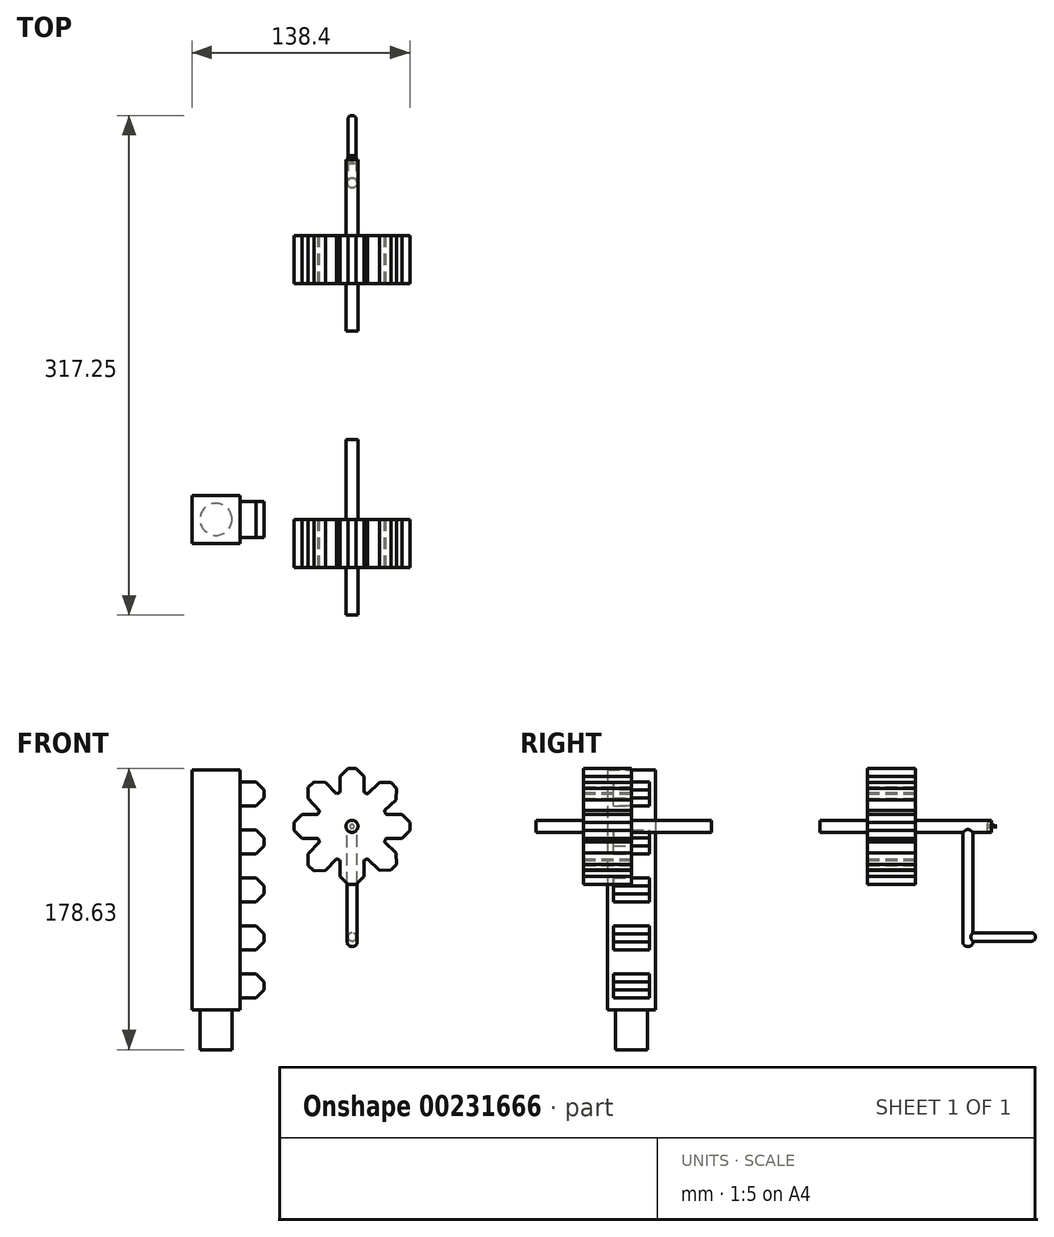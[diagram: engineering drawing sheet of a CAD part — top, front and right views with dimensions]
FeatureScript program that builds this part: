
annotation { "Feature Type Name" : "Feature", "Feature Type Description" : "" }
export const myFeature = defineFeature(function(context is Context, id is Id, definition is map)
    precondition{}
    {
        {
            var Q0;
            Q0=qCreatedBy(makeId("Top.planeOp"),FACE);
            var sketch = newSketch(context, id + "F0", { "sketchPlane" : qUnion([Q0])});
            skLineSegment(sketch, "E0.bottom", {"start": v(-15.24, -15.24) * mm, "end": v(15.24, -15.24) * mm});
            skLineSegment(sketch, "E0.top", {"start": v(-15.24, 15.24) * mm, "end": v(15.24, 15.24) * mm});
            skLineSegment(sketch, "E0.left", {"start": v(-15.24, -15.24) * mm, "end": v(-15.24, 15.24) * mm});
            skLineSegment(sketch, "E0.right", {"start": v(15.24, -15.24) * mm, "end": v(15.24, 15.24) * mm});
            skPoint(sketch, "E0.middle", {"position": v(0, 0) * mm});
            skCircle(sketch, "E1", {"center": v(0, 0) * mm, "radius": 10.16 * mm});
            skSolve(sketch);
        }
        {
            var Q0;
            Q0=makeQuery(id+"F0.imprint","IMPRINT",FACE,{"disambiguationData":[TD([[makeQuery(id+"F0.imprint","IMPRINT",EDGE,{"derivedFrom":sQuery(id+"F0.wireOp",EDGE,"E0.bottom")}),1.0]])]});
            var Q1;
            Q1=makeQuery(id+"F0.imprint","IMPRINT",FACE,{"disambiguationData":[TD([[makeQuery(id+"F0.imprint","IMPRINT",EDGE,{"derivedFrom":sQuery(id+"F0.wireOp",EDGE,"E1")}),1.0]])]});
            extrude(context, id + "F1", {"entities" : qUnion([Q0, Q1]), "depth" : 152.4 * mm});
        }
        {
            var Q0;
            Q0=makeQuery(id+"F0.imprint","IMPRINT",FACE,{"disambiguationData":[TD([[makeQuery(id+"F0.imprint","IMPRINT",EDGE,{"derivedFrom":sQuery(id+"F0.wireOp",EDGE,"E1")}),1.0]])]});
            extrude(context, id + "F2", {"entities" : qUnion([Q0]), "operationType" : NewBodyOperationType.ADD, "oppositeDirection" : true, "depth" : 25.4 * mm});
        }
        {
            var Q0;
            Q0=qCreatedBy(makeId("Right.planeOp"),FACE);
            var sketch = newSketch(context, id + "F3", { "sketchPlane" : qUnion([Q0])});
            skLineSegment(sketch, "E2.bottom", {"start": v(-11.43, 7.62) * mm, "end": v(11.43, 7.62) * mm});
            skLineSegment(sketch, "E2.top", {"start": v(-11.43, 22.86) * mm, "end": v(11.43, 22.86) * mm});
            skLineSegment(sketch, "E2.left", {"start": v(-11.43, 7.62) * mm, "end": v(-11.43, 22.86) * mm});
            skLineSegment(sketch, "E2.right", {"start": v(11.43, 7.62) * mm, "end": v(11.43, 22.86) * mm});
            skPoint(sketch, "E2.middle", {"position": v(0, 15.24) * mm});
            skLineSegment(sketch, "E3.0.1.0", {"start": v(-11.43, 53.34) * mm, "end": v(11.43, 53.34) * mm});
            skLineSegment(sketch, "E3.0.1.1", {"start": v(-11.43, 38.1) * mm, "end": v(-11.43, 53.34) * mm});
            skLineSegment(sketch, "E3.0.1.2", {"start": v(11.43, 38.1) * mm, "end": v(11.43, 53.34) * mm});
            skLineSegment(sketch, "E3.0.1.3", {"start": v(-11.43, 38.1) * mm, "end": v(11.43, 38.1) * mm});
            skLineSegment(sketch, "E3.0.2.0", {"start": v(-11.43, 83.82) * mm, "end": v(11.43, 83.82) * mm});
            skLineSegment(sketch, "E3.0.2.1", {"start": v(-11.43, 68.58) * mm, "end": v(-11.43, 83.82) * mm});
            skLineSegment(sketch, "E3.0.2.2", {"start": v(11.43, 68.58) * mm, "end": v(11.43, 83.82) * mm});
            skLineSegment(sketch, "E3.0.2.3", {"start": v(-11.43, 68.58) * mm, "end": v(11.43, 68.58) * mm});
            skLineSegment(sketch, "E3.0.3.0", {"start": v(-11.43, 114.3) * mm, "end": v(11.43, 114.3) * mm});
            skLineSegment(sketch, "E3.0.3.1", {"start": v(-11.43, 99.06) * mm, "end": v(-11.43, 114.3) * mm});
            skLineSegment(sketch, "E3.0.3.2", {"start": v(11.43, 99.06) * mm, "end": v(11.43, 114.3) * mm});
            skLineSegment(sketch, "E3.0.3.3", {"start": v(-11.43, 99.06) * mm, "end": v(11.43, 99.06) * mm});
            skLineSegment(sketch, "E3.0.4.0", {"start": v(-11.43, 144.78) * mm, "end": v(11.43, 144.78) * mm});
            skLineSegment(sketch, "E3.0.4.1", {"start": v(-11.43, 129.54) * mm, "end": v(-11.43, 144.78) * mm});
            skLineSegment(sketch, "E3.0.4.2", {"start": v(11.43, 129.54) * mm, "end": v(11.43, 144.78) * mm});
            skLineSegment(sketch, "E3.0.4.3", {"start": v(-11.43, 129.54) * mm, "end": v(11.43, 129.54) * mm});
            skLineSegment(sketch, "E3.direction1", {"start": v(-11.43, 22.86) * mm, "end": v(13.97, 22.86) * mm, "construction": true});
            skLineSegment(sketch, "E3.direction2", {"start": v(-11.43, 38.1) * mm, "end": v(-11.43, 53.34) * mm, "construction": true});
            skSolve(sketch);
        }
        {
            var Q0;
            Q0 = qSketchRegion(id + "F3", true);
            extrude(context, id + "F4", {"entities" : qUnion([Q0]), "operationType" : NewBodyOperationType.ADD, "depth" : 30.48 * mm});
        }
        {
            var Q0;
            Q0=makeQuery(id+"F4.opExtrude","CAP_EDGE",EDGE,{"disambiguationData":[OSD([sQuery(id+"F3.wireOp",EDGE,"E2.top")])],"isStart":false});
            var Q1;
            Q1=makeQuery(id+"F4.opExtrude","CAP_EDGE",EDGE,{"disambiguationData":[OSD([sQuery(id+"F3.wireOp",EDGE,"E2.bottom")])],"isStart":false});
            var Q2;
            Q2=makeQuery(id+"F4.opExtrude","CAP_EDGE",EDGE,{"disambiguationData":[OSD([sQuery(id+"F3.wireOp",EDGE,"E3.0.1.0")])],"isStart":false});
            var Q3;
            Q3=makeQuery(id+"F4.opExtrude","CAP_EDGE",EDGE,{"disambiguationData":[OSD([sQuery(id+"F3.wireOp",EDGE,"E3.0.1.3")])],"isStart":false});
            var Q4;
            Q4=makeQuery(id+"F4.opExtrude","CAP_EDGE",EDGE,{"disambiguationData":[OSD([sQuery(id+"F3.wireOp",EDGE,"E3.0.2.0")])],"isStart":false});
            var Q5;
            Q5=makeQuery(id+"F4.opExtrude","CAP_EDGE",EDGE,{"disambiguationData":[OSD([sQuery(id+"F3.wireOp",EDGE,"E3.0.2.3")])],"isStart":false});
            var Q6;
            Q6=makeQuery(id+"F4.opExtrude","CAP_EDGE",EDGE,{"disambiguationData":[OSD([sQuery(id+"F3.wireOp",EDGE,"E3.0.3.0")])],"isStart":false});
            var Q7;
            Q7=makeQuery(id+"F4.opExtrude","CAP_EDGE",EDGE,{"disambiguationData":[OSD([sQuery(id+"F3.wireOp",EDGE,"E3.0.3.3")])],"isStart":false});
            var Q8;
            Q8=makeQuery(id+"F4.opExtrude","CAP_EDGE",EDGE,{"disambiguationData":[OSD([sQuery(id+"F3.wireOp",EDGE,"E3.0.4.0")])],"isStart":false});
            var Q9;
            Q9=makeQuery(id+"F4.opExtrude","CAP_EDGE",EDGE,{"disambiguationData":[OSD([sQuery(id+"F3.wireOp",EDGE,"E3.0.4.3")])],"isStart":false});
            chamfer(context, id + "F5", {"entities" : qUnion([Q0, Q1, Q2, Q3, Q4, Q5, Q6, Q7, Q8, Q9]), "width" : 5.08 * mm, "tangentPropagation" : true});
        }
        {
            var Q0;
            Q0=qCreatedBy(makeId("Front.planeOp"),FACE);
            var sketch = newSketch(context, id + "F6", { "sketchPlane" : qUnion([Q0])});
            skCircle(sketch, "E4", {"center": v(86.36, 116.44) * mm, "radius": 22.86 * mm});
            skLineSegment(sketch, "E5", {"start": v(93.98, 138) * mm, "end": v(93.98, 153.23) * mm});
            skLineSegment(sketch, "E6", {"start": v(93.98, 153.23) * mm, "end": v(78.74, 153.23) * mm});
            skLineSegment(sketch, "E7", {"start": v(78.74, 153.23) * mm, "end": v(78.74, 138) * mm});
            skLineSegment(sketch, "E8", {"start": v(86.36, 116.44) * mm, "end": v(41.12, 116.44) * mm, "construction": true});
            skLineSegment(sketch, "E9", {"start": v(41.12, 116.44) * mm, "end": v(122.57, 116.44) * mm, "construction": true});
            skLineSegment(sketch, "E10.MirrorCS", {"start": v(93.98, 79.65) * mm, "end": v(78.74, 79.65) * mm});
            skLineSegment(sketch, "E11.MirrorCS", {"start": v(78.74, 79.65) * mm, "end": v(78.74, 94.89) * mm});
            skLineSegment(sketch, "E12.MirrorCS", {"start": v(93.98, 94.89) * mm, "end": v(93.98, 79.65) * mm});
            skLineSegment(sketch, "E13", {"start": v(64.8, 124) * mm, "end": v(49.55, 124) * mm});
            skLineSegment(sketch, "E14", {"start": v(49.55, 124) * mm, "end": v(49.55, 108.76) * mm});
            skLineSegment(sketch, "E15", {"start": v(49.55, 108.76) * mm, "end": v(64.83, 108.76) * mm});
            skLineSegment(sketch, "E16", {"start": v(86.36, 116.44) * mm, "end": v(86.36, 160.8) * mm, "construction": true});
            skLineSegment(sketch, "E17", {"start": v(86.36, 160.8) * mm, "end": v(86.36, 67.55) * mm, "construction": true});
            skLineSegment(sketch, "E18", {"start": v(86.36, 116.44) * mm, "end": v(44.44, 158.37) * mm, "construction": true});
            skLineSegment(sketch, "E19", {"start": v(44.44, 158.37) * mm, "end": v(124.8, 78.01) * mm, "construction": true});
            skLineSegment(sketch, "E20.MirrorCS", {"start": v(107.92, 108.82) * mm, "end": v(123.16, 108.82) * mm});
            skLineSegment(sketch, "E21.MirrorCS", {"start": v(123.16, 108.82) * mm, "end": v(123.16, 124.06) * mm});
            skLineSegment(sketch, "E22.MirrorCS", {"start": v(123.16, 124.06) * mm, "end": v(107.92, 124.06) * mm});
            skLineSegment(sketch, "E23", {"start": v(106.94, 126.4) * mm, "end": v(118.1, 136.8) * mm});
            skLineSegment(sketch, "E24", {"start": v(118.1, 136.8) * mm, "end": v(107.7, 147.94) * mm});
            skLineSegment(sketch, "E25", {"start": v(107.7, 147.94) * mm, "end": v(96.1, 137.12) * mm});
            skPoint(sketch, "E26.orphan", {"position": v(109.22, 153.23) * mm});
            skPoint(sketch, "E27.MirrorCS.end.orphan", {"position": v(109.22, 138) * mm});
            skPoint(sketch, "E28.MirrorCS.start.orphan", {"position": v(93.98, 153.23) * mm});
            skLineSegment(sketch, "E29.MirrorCS", {"start": v(54.87, 95.1) * mm, "end": v(65.68, 106.7) * mm});
            skLineSegment(sketch, "E30.MirrorCS", {"start": v(66.01, 84.71) * mm, "end": v(54.87, 95.1) * mm});
            skLineSegment(sketch, "E31.MirrorCS", {"start": v(76.4, 95.87) * mm, "end": v(66.01, 84.71) * mm});
            skLineSegment(sketch, "E32.MirrorCS", {"start": v(54.87, 137.77) * mm, "end": v(65.68, 126.18) * mm});
            skLineSegment(sketch, "E33.MirrorCS", {"start": v(76.4, 137.02) * mm, "end": v(66.01, 148.17) * mm});
            skLineSegment(sketch, "E34.MirrorCS", {"start": v(66.01, 148.17) * mm, "end": v(54.87, 137.77) * mm});
            skLineSegment(sketch, "E35.MirrorCS", {"start": v(106.94, 106.48) * mm, "end": v(118.1, 96.1) * mm});
            skLineSegment(sketch, "E36.MirrorCS", {"start": v(118.1, 96.1) * mm, "end": v(107.7, 84.95) * mm});
            skLineSegment(sketch, "E37.MirrorCS", {"start": v(107.7, 84.95) * mm, "end": v(96.1, 95.76) * mm});
            skCircle(sketch, "E38", {"center": v(86.36, 116.44) * mm, "radius": 3.81 * mm});
            skSolve(sketch);
        }
        {
            var Q0;
            {var subQ0=sQuery(id+"F6.wireOp",EDGE,"E4");var subQ1=makeQuery(id+"F6.imprint","INTERSECT",VERTEX,{"derivedFrom":[subQ0,sQuery(id+"F6.wireOp",EDGE,"E5")]});Q0=makeQuery(id+"F6.imprint","IMPRINT",FACE,{"disambiguationData":[TD([[makeQuery(id+"F6.imprint","IMPRINT",EDGE,{"disambiguationData":[TD([[subQ1,-1.0]])],"derivedFrom":subQ0}),1.0]])]});}
            var Q1;
            {var subQ0=sQuery(id+"F6.wireOp",EDGE,"E5");Q1=makeQuery(id+"F6.imprint","IMPRINT",FACE,{"disambiguationData":[TD([[makeQuery(id+"F6.imprint","IMPRINT",EDGE,{"derivedFrom":subQ0}),1.0]])]});}
            var Q2;
            {var subQ0=sQuery(id+"F6.wireOp",EDGE,"E23");Q2=makeQuery(id+"F6.imprint","IMPRINT",FACE,{"disambiguationData":[TD([[makeQuery(id+"F6.imprint","IMPRINT",EDGE,{"derivedFrom":subQ0}),1.0]])]});}
            var Q3;
            {var subQ0=sQuery(id+"F6.wireOp",EDGE,"E32.MirrorCS");Q3=makeQuery(id+"F6.imprint","IMPRINT",FACE,{"disambiguationData":[TD([[makeQuery(id+"F6.imprint","IMPRINT",EDGE,{"derivedFrom":subQ0}),1.0]])]});}
            var Q4;
            {var subQ0=sQuery(id+"F6.wireOp",EDGE,"E13");Q4=makeQuery(id+"F6.imprint","IMPRINT",FACE,{"disambiguationData":[TD([[makeQuery(id+"F6.imprint","IMPRINT",EDGE,{"derivedFrom":subQ0}),1.0]])]});}
            var Q5;
            {var subQ0=sQuery(id+"F6.wireOp",EDGE,"E29.MirrorCS");Q5=makeQuery(id+"F6.imprint","IMPRINT",FACE,{"disambiguationData":[TD([[makeQuery(id+"F6.imprint","IMPRINT",EDGE,{"derivedFrom":subQ0}),-1.0]])]});}
            var Q6;
            Q6=makeQuery(id+"F6.imprint","IMPRINT",FACE,{"disambiguationData":[TD([[makeQuery(id+"F6.imprint","IMPRINT",EDGE,{"derivedFrom":sQuery(id+"F6.wireOp",EDGE,"E10.MirrorCS")}),-1.0]])]});
            var Q7;
            {var subQ0=sQuery(id+"F6.wireOp",EDGE,"E20.MirrorCS");Q7=makeQuery(id+"F6.imprint","IMPRINT",FACE,{"disambiguationData":[TD([[makeQuery(id+"F6.imprint","IMPRINT",EDGE,{"derivedFrom":subQ0}),1.0]])]});}
            var Q8;
            {var subQ0=sQuery(id+"F6.wireOp",EDGE,"E35.MirrorCS");Q8=makeQuery(id+"F6.imprint","IMPRINT",FACE,{"disambiguationData":[TD([[makeQuery(id+"F6.imprint","IMPRINT",EDGE,{"derivedFrom":subQ0}),-1.0]])]});}
            extrude(context, id + "F7", {"entities" : qUnion([Q0, Q1, Q2, Q3, Q4, Q5, Q6, Q7, Q8]), "depth" : 30.48 * mm});
        }
        {
            var Q0;
            Q0=makeQuery(id+"F7.opExtrude","SWEPT_EDGE",EDGE,{"disambiguationData":[OSD([sQuery(id+"F6.wireOp",EDGE,"E6"),sQuery(id+"F6.wireOp",EDGE,"E7")])]});
            var Q1;
            Q1=makeQuery(id+"F7.opExtrude","SWEPT_EDGE",EDGE,{"disambiguationData":[OSD([sQuery(id+"F6.wireOp",EDGE,"E5"),sQuery(id+"F6.wireOp",EDGE,"E6")])]});
            chamfer(context, id + "F8", {"entities" : qUnion([Q0, Q1]), "width" : 5.08 * mm, "tangentPropagation" : true});
        }
        {
            var Q0;
            Q0=makeQuery(id+"F7.opExtrude","SWEPT_EDGE",EDGE,{"disambiguationData":[OSD([sQuery(id+"F6.wireOp",EDGE,"E24"),sQuery(id+"F6.wireOp",EDGE,"E25")])]});
            var Q1;
            Q1=makeQuery(id+"F7.opExtrude","SWEPT_EDGE",EDGE,{"disambiguationData":[OSD([sQuery(id+"F6.wireOp",EDGE,"E23"),sQuery(id+"F6.wireOp",EDGE,"E24")])]});
            var Q2;
            Q2=makeQuery(id+"F7.opExtrude","SWEPT_EDGE",EDGE,{"disambiguationData":[OSD([sQuery(id+"F6.wireOp",EDGE,"E21.MirrorCS"),sQuery(id+"F6.wireOp",EDGE,"E22.MirrorCS")])]});
            var Q3;
            Q3=makeQuery(id+"F7.opExtrude","SWEPT_EDGE",EDGE,{"disambiguationData":[OSD([sQuery(id+"F6.wireOp",EDGE,"E20.MirrorCS"),sQuery(id+"F6.wireOp",EDGE,"E21.MirrorCS")])]});
            var Q4;
            Q4=makeQuery(id+"F7.opExtrude","SWEPT_EDGE",EDGE,{"disambiguationData":[OSD([sQuery(id+"F6.wireOp",EDGE,"E35.MirrorCS"),sQuery(id+"F6.wireOp",EDGE,"E36.MirrorCS")])]});
            var Q5;
            Q5=makeQuery(id+"F7.opExtrude","SWEPT_EDGE",EDGE,{"disambiguationData":[OSD([sQuery(id+"F6.wireOp",EDGE,"E36.MirrorCS"),sQuery(id+"F6.wireOp",EDGE,"E37.MirrorCS")])]});
            var Q6;
            Q6=makeQuery(id+"F7.opExtrude","SWEPT_EDGE",EDGE,{"disambiguationData":[OSD([sQuery(id+"F6.wireOp",EDGE,"E10.MirrorCS"),sQuery(id+"F6.wireOp",EDGE,"E12.MirrorCS")])]});
            var Q7;
            Q7=makeQuery(id+"F7.opExtrude","SWEPT_EDGE",EDGE,{"disambiguationData":[OSD([sQuery(id+"F6.wireOp",EDGE,"E10.MirrorCS"),sQuery(id+"F6.wireOp",EDGE,"E11.MirrorCS")])]});
            var Q8;
            Q8=makeQuery(id+"F7.opExtrude","SWEPT_EDGE",EDGE,{"disambiguationData":[OSD([sQuery(id+"F6.wireOp",EDGE,"E30.MirrorCS"),sQuery(id+"F6.wireOp",EDGE,"E31.MirrorCS")])]});
            var Q9;
            Q9=makeQuery(id+"F7.opExtrude","SWEPT_EDGE",EDGE,{"disambiguationData":[OSD([sQuery(id+"F6.wireOp",EDGE,"E29.MirrorCS"),sQuery(id+"F6.wireOp",EDGE,"E30.MirrorCS")])]});
            var Q10;
            Q10=makeQuery(id+"F7.opExtrude","SWEPT_EDGE",EDGE,{"disambiguationData":[OSD([sQuery(id+"F6.wireOp",EDGE,"E13"),sQuery(id+"F6.wireOp",EDGE,"E14")])]});
            var Q11;
            Q11=makeQuery(id+"F7.opExtrude","SWEPT_EDGE",EDGE,{"disambiguationData":[OSD([sQuery(id+"F6.wireOp",EDGE,"E14"),sQuery(id+"F6.wireOp",EDGE,"E15")])]});
            var Q12;
            Q12=makeQuery(id+"F7.opExtrude","SWEPT_EDGE",EDGE,{"disambiguationData":[OSD([sQuery(id+"F6.wireOp",EDGE,"E32.MirrorCS"),sQuery(id+"F6.wireOp",EDGE,"E34.MirrorCS")])]});
            var Q13;
            Q13=makeQuery(id+"F7.opExtrude","SWEPT_EDGE",EDGE,{"disambiguationData":[OSD([sQuery(id+"F6.wireOp",EDGE,"E33.MirrorCS"),sQuery(id+"F6.wireOp",EDGE,"E34.MirrorCS")])]});
            chamfer(context, id + "F9", {"entities" : qUnion([Q0, Q1, Q2, Q3, Q4, Q5, Q6, Q7, Q8, Q9, Q10, Q11, Q12, Q13]), "width" : 5.08 * mm, "tangentPropagation" : true});
        }
        {
            var Q0;
            Q0=makeQuery(id+"F6.imprint","IMPRINT",FACE,{"disambiguationData":[TD([[makeQuery(id+"F6.imprint","IMPRINT",EDGE,{"derivedFrom":sQuery(id+"F6.wireOp",EDGE,"E38")}),1.0]])]});
            extrude(context, id + "F10", {"entities" : qUnion([Q0]), "operationType" : NewBodyOperationType.ADD, "depth" : 60.7 * mm, "hasSecondDirection" : true, "secondDirectionOppositeDirection" : true, "secondDirectionDepth" : 50.8 * mm});
        }
        {
            var Q0;
            Q0=makeQuery(id+"F7.opExtrude","SWEPT_BODY",BODY,{"disambiguationData":[OSD([sQuery(id+"F6.wireOp",EDGE,"E4"),sQuery(id+"F6.wireOp",EDGE,"E5"),sQuery(id+"F6.wireOp",EDGE,"E6"),sQuery(id+"F6.wireOp",EDGE,"E7"),sQuery(id+"F6.wireOp",EDGE,"E10.MirrorCS"),sQuery(id+"F6.wireOp",EDGE,"E11.MirrorCS"),sQuery(id+"F6.wireOp",EDGE,"E12.MirrorCS"),sQuery(id+"F6.wireOp",EDGE,"E13"),sQuery(id+"F6.wireOp",EDGE,"E14"),sQuery(id+"F6.wireOp",EDGE,"E15"),sQuery(id+"F6.wireOp",EDGE,"E20.MirrorCS"),sQuery(id+"F6.wireOp",EDGE,"E21.MirrorCS"),sQuery(id+"F6.wireOp",EDGE,"E22.MirrorCS"),sQuery(id+"F6.wireOp",EDGE,"E23"),sQuery(id+"F6.wireOp",EDGE,"E24"),sQuery(id+"F6.wireOp",EDGE,"E25"),sQuery(id+"F6.wireOp",EDGE,"E29.MirrorCS"),sQuery(id+"F6.wireOp",EDGE,"E30.MirrorCS"),sQuery(id+"F6.wireOp",EDGE,"E31.MirrorCS"),sQuery(id+"F6.wireOp",EDGE,"E32.MirrorCS"),sQuery(id+"F6.wireOp",EDGE,"E33.MirrorCS"),sQuery(id+"F6.wireOp",EDGE,"E34.MirrorCS"),sQuery(id+"F6.wireOp",EDGE,"E35.MirrorCS"),sQuery(id+"F6.wireOp",EDGE,"E36.MirrorCS"),sQuery(id+"F6.wireOp",EDGE,"E37.MirrorCS"),sQuery(id+"F6.wireOp",EDGE,"E38")])]});
            transform(context, id + "F11", {"entities" : qUnion([Q0]), "transformType" : TransformType.TRANSLATION_3D, "dx" : 0 * mm, "dy" : 180.34 * mm, "dz" : 0 * mm, "makeCopy" : true});
        }
        {
            var Q0;
            Q0=makeQuery(id+"F11.opPattern","COPY",FACE,{"derivedFrom":makeQuery(id+"F7.opExtrude","SWEPT_FACE",FACE,{"disambiguationData":[OSD([sQuery(id+"F6.wireOp",EDGE,"E20.MirrorCS")])]}),"instanceName":"1"});
            cPlane(context, id + "F12", {"entities" : qUnion([Q0]), "cplaneType" : CPlaneType.OFFSET, "offset" : 7.62 * mm, "oppositeDirection" : true, "width" : 152.4 * mm, "height" : 152.4 * mm});
        }
        {
            var Q0;
            Q0=qCreatedBy(id+"F12.planeOp",FACE);
            var sketch = newSketch(context, id + "F13", { "sketchPlane" : qUnion([Q0])});
            skCircle(sketch, "E39", {"center": v(86.5, -213.67) * mm, "radius": 3.12 * mm});
            skSolve(sketch);
        }
        {
            var Q0;
            Q0 = qSketchRegion(id + "F13", true);
            extrude(context, id + "F14", {"entities" : qUnion([Q0]), "operationType" : NewBodyOperationType.ADD, "depth" : 76.2 * mm});
        }
        {
            var Q0;
            Q0=makeQuery(id+"F11.opPattern","COPY",EDGE,{"derivedFrom":makeQuery(id+"F10.opExtrude","CAP_EDGE",EDGE,{"disambiguationData":[OSD([sQuery(id+"F6.wireOp",EDGE,"E38")])],"isStart":true}),"instanceName":"1"});
            var Q1;
            Q1=makeQuery(id+"F14.opExtrude","CAP_EDGE",EDGE,{"disambiguationData":[OSD([sQuery(id+"F13.wireOp",EDGE,"E39")])],"isStart":true});
            var Q2;
            Q2=makeQuery(id+"F14.opExtrude","CAP_EDGE",EDGE,{"disambiguationData":[OSD([sQuery(id+"F13.wireOp",EDGE,"E39")])],"isStart":false});
            fillet(context, id + "F15", {"entities" : qUnion([Q0, Q1, Q2]), "radius" : 2.54 * mm, "tangentPropagation" : true, "allowEdgeOverflow" : false});
        }
        {
            var Q0;
            Q0=makeQuery(id+"F11.opPattern","COPY",FACE,{"derivedFrom":makeQuery(id+"F7.opExtrude","CAP_FACE",FACE,{"disambiguationData":[OSD([sQuery(id+"F6.wireOp",EDGE,"E4"),sQuery(id+"F6.wireOp",EDGE,"E5"),sQuery(id+"F6.wireOp",EDGE,"E6"),sQuery(id+"F6.wireOp",EDGE,"E7"),sQuery(id+"F6.wireOp",EDGE,"E10.MirrorCS"),sQuery(id+"F6.wireOp",EDGE,"E11.MirrorCS"),sQuery(id+"F6.wireOp",EDGE,"E12.MirrorCS"),sQuery(id+"F6.wireOp",EDGE,"E13"),sQuery(id+"F6.wireOp",EDGE,"E14"),sQuery(id+"F6.wireOp",EDGE,"E15"),sQuery(id+"F6.wireOp",EDGE,"E20.MirrorCS"),sQuery(id+"F6.wireOp",EDGE,"E21.MirrorCS"),sQuery(id+"F6.wireOp",EDGE,"E22.MirrorCS"),sQuery(id+"F6.wireOp",EDGE,"E23"),sQuery(id+"F6.wireOp",EDGE,"E24"),sQuery(id+"F6.wireOp",EDGE,"E25"),sQuery(id+"F6.wireOp",EDGE,"E29.MirrorCS"),sQuery(id+"F6.wireOp",EDGE,"E30.MirrorCS"),sQuery(id+"F6.wireOp",EDGE,"E31.MirrorCS"),sQuery(id+"F6.wireOp",EDGE,"E32.MirrorCS"),sQuery(id+"F6.wireOp",EDGE,"E33.MirrorCS"),sQuery(id+"F6.wireOp",EDGE,"E34.MirrorCS"),sQuery(id+"F6.wireOp",EDGE,"E35.MirrorCS"),sQuery(id+"F6.wireOp",EDGE,"E36.MirrorCS"),sQuery(id+"F6.wireOp",EDGE,"E37.MirrorCS"),sQuery(id+"F6.wireOp",EDGE,"E38")])],"isStart":true}),"instanceName":"1"});
            cPlane(context, id + "F16", {"entities" : qUnion([Q0]), "cplaneType" : CPlaneType.OFFSET, "offset" : 33.02 * mm, "width" : 152.4 * mm, "height" : 152.4 * mm});
        }
        {
            var Q0;
            Q0=qCreatedBy(id+"F16.planeOp",FACE);
            var sketch = newSketch(context, id + "F17", { "sketchPlane" : qUnion([Q0])});
            skCircle(sketch, "E40", {"center": v(-86.41, 46.15) * mm, "radius": 2.67 * mm});
            skSolve(sketch);
        }
        {
            var Q0;
            Q0 = qSketchRegion(id + "F17", true);
            extrude(context, id + "F18", {"entities" : qUnion([Q0]), "operationType" : NewBodyOperationType.ADD, "depth" : 43.18 * mm});
        }
        {
            var Q0;
            Q0=makeQuery(id+"F18.opExtrude","CAP_EDGE",EDGE,{"disambiguationData":[OSD([sQuery(id+"F17.wireOp",EDGE,"E40")])],"isStart":false});
            fillet(context, id + "F19", {"entities" : qUnion([Q0]), "radius" : 2.54 * mm, "tangentPropagation" : true, "allowEdgeOverflow" : false});
        }
    });
